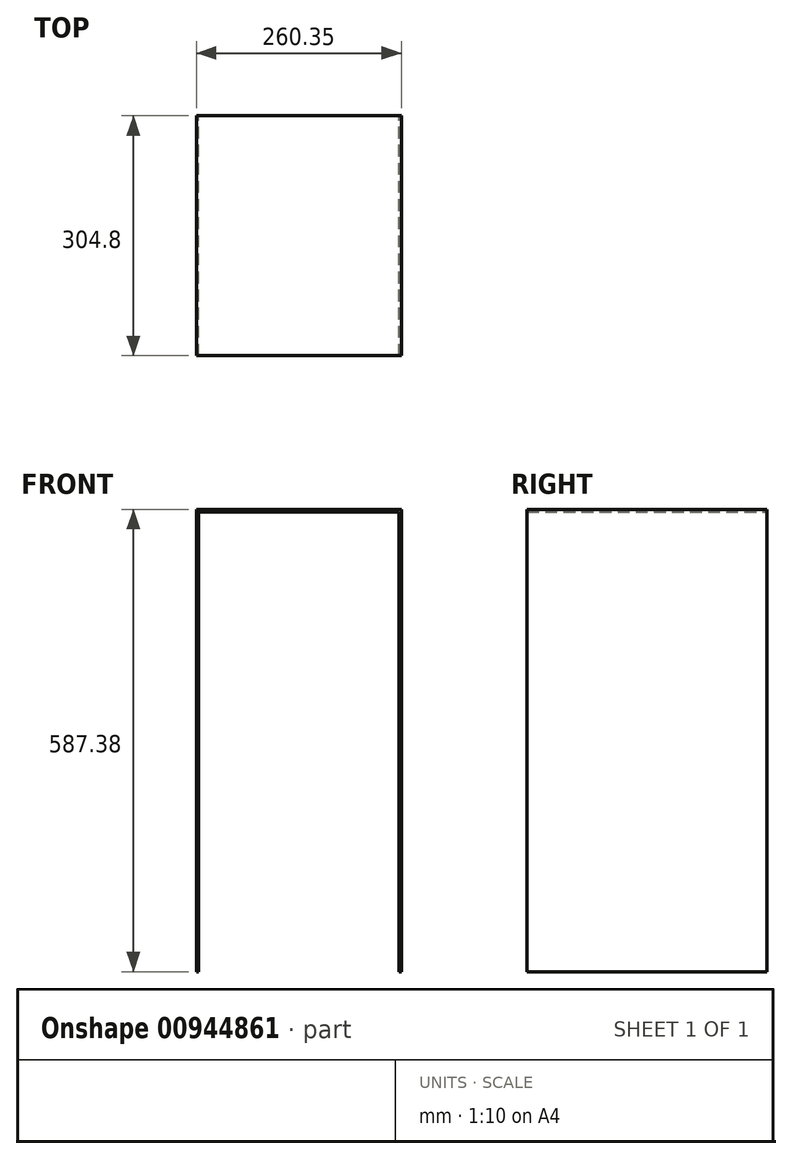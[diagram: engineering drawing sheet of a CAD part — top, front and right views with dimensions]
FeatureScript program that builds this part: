
annotation { "Feature Type Name" : "Feature", "Feature Type Description" : "" }
export const myFeature = defineFeature(function(context is Context, id is Id, definition is map)
    precondition{}
    {
        {
            var Q0;
            Q0=qCreatedBy(makeId("Front.planeOp"),FACE);
            var sketch = newSketch(context, id + "F0", { "sketchPlane" : qUnion([Q0])});
            skSolve(sketch);
        }
        {
            var Q0;
            Q0=qCreatedBy(makeId("Front.planeOp"),FACE);
            var sketch = newSketch(context, id + "F1", { "sketchPlane" : qUnion([Q0])});
            skLineSegment(sketch, "E0", {"start": v(-181.43, 0) * mm, "end": v(-181.43, 587.38) * mm});
            skLineSegment(sketch, "E1", {"start": v(-181.43, 587.38) * mm, "end": v(78.92, 587.38) * mm});
            skLineSegment(sketch, "E2", {"start": v(78.92, 587.38) * mm, "end": v(78.92, 0) * mm});
            skLineSegment(sketch, "E3.0", {"start": v(75.75, 584.2) * mm, "end": v(75.75, 0) * mm});
            skLineSegment(sketch, "E3.1", {"start": v(-178.25, 584.2) * mm, "end": v(75.75, 584.2) * mm});
            skLineSegment(sketch, "E3.2", {"start": v(-178.25, 0) * mm, "end": v(-178.25, 584.2) * mm});
            skLineSegment(sketch, "E4", {"start": v(-181.43, 0) * mm, "end": v(-178.25, 0) * mm});
            skLineSegment(sketch, "E5", {"start": v(75.75, 0) * mm, "end": v(78.92, 0) * mm});
            skSolve(sketch);
        }
        {
            var Q0;
            Q0 = qSketchRegion(id + "F0", true);
            var Q1;
            Q1=makeQuery(id+"F1.imprint","IMPRINT",FACE,{"disambiguationData":[TD([[makeQuery(id+"F1.imprint","IMPRINT",EDGE,{"derivedFrom":sQuery(id+"F1.wireOp",EDGE,"E0")}),-1.0]])]});
            extrude(context, id + "F2", {"entities" : qUnion([Q0, Q1]), "depth" : 304.8 * mm, "offsetDistance" : 25.4 * mm});
        }
    });
